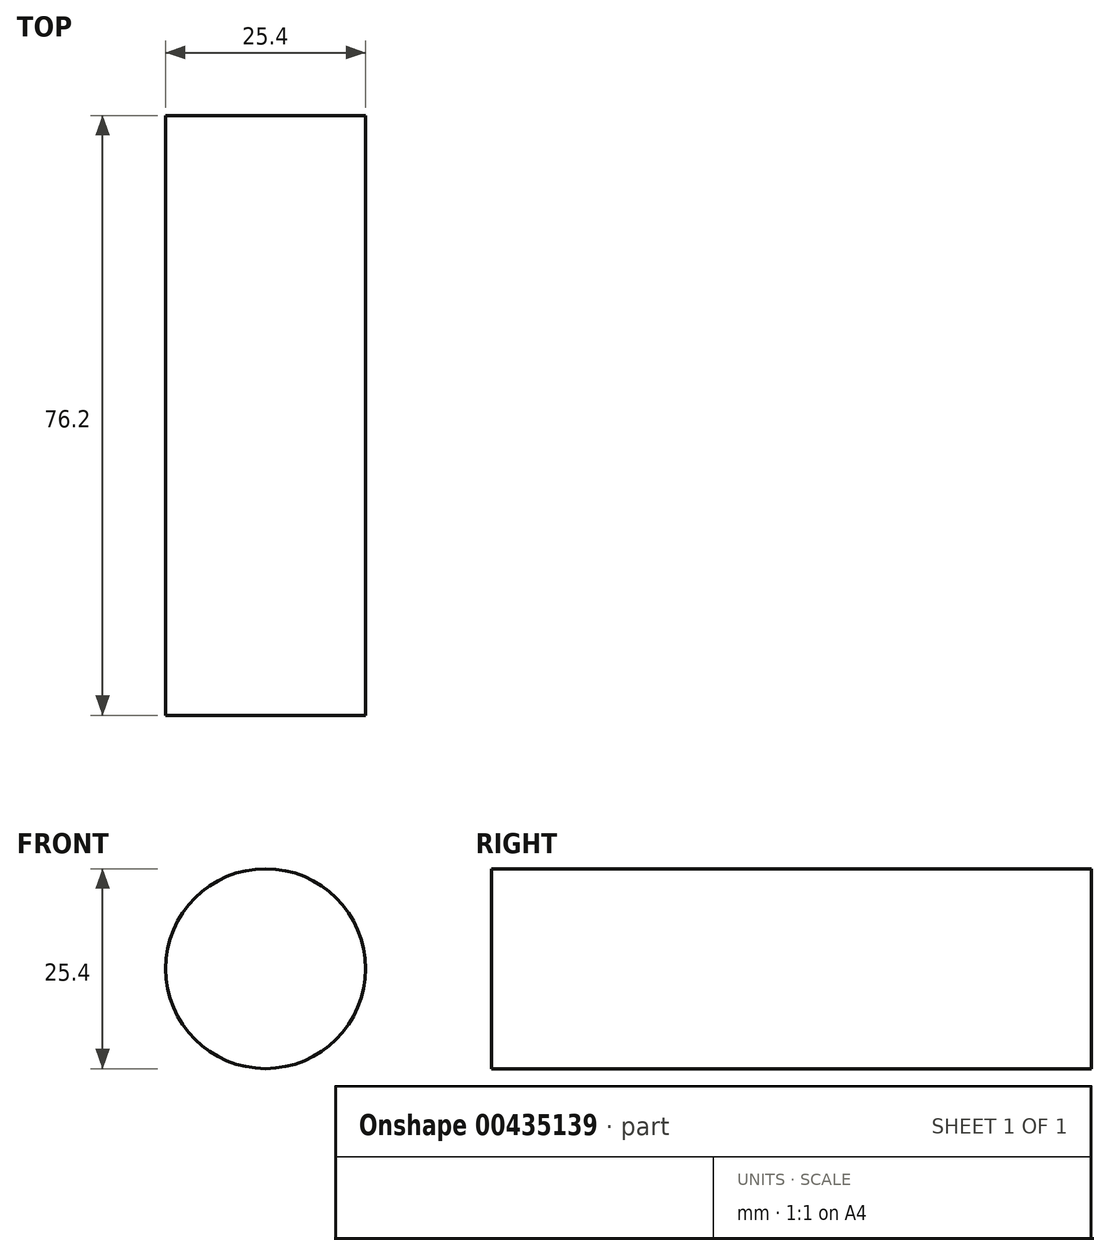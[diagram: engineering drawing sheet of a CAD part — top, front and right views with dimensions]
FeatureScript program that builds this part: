
annotation { "Feature Type Name" : "Feature", "Feature Type Description" : "" }
export const myFeature = defineFeature(function(context is Context, id is Id, definition is map)
    precondition{}
    {
        {
            var Q0;
            Q0=qCreatedBy(makeId("Front.planeOp"),FACE);
            var sketch = newSketch(context, id + "F0", { "sketchPlane" : qUnion([Q0])});
            skCircle(sketch, "E0", {"center": v(-4.2, 46.78) * mm, "radius": 12.7 * mm});
            skSolve(sketch);
        }
        {
            var Q0;
            Q0 = qSketchRegion(id + "F0", true);
            extrude(context, id + "F1", {"entities" : qUnion([Q0]), "depth" : 76.2 * mm});
        }
    });
